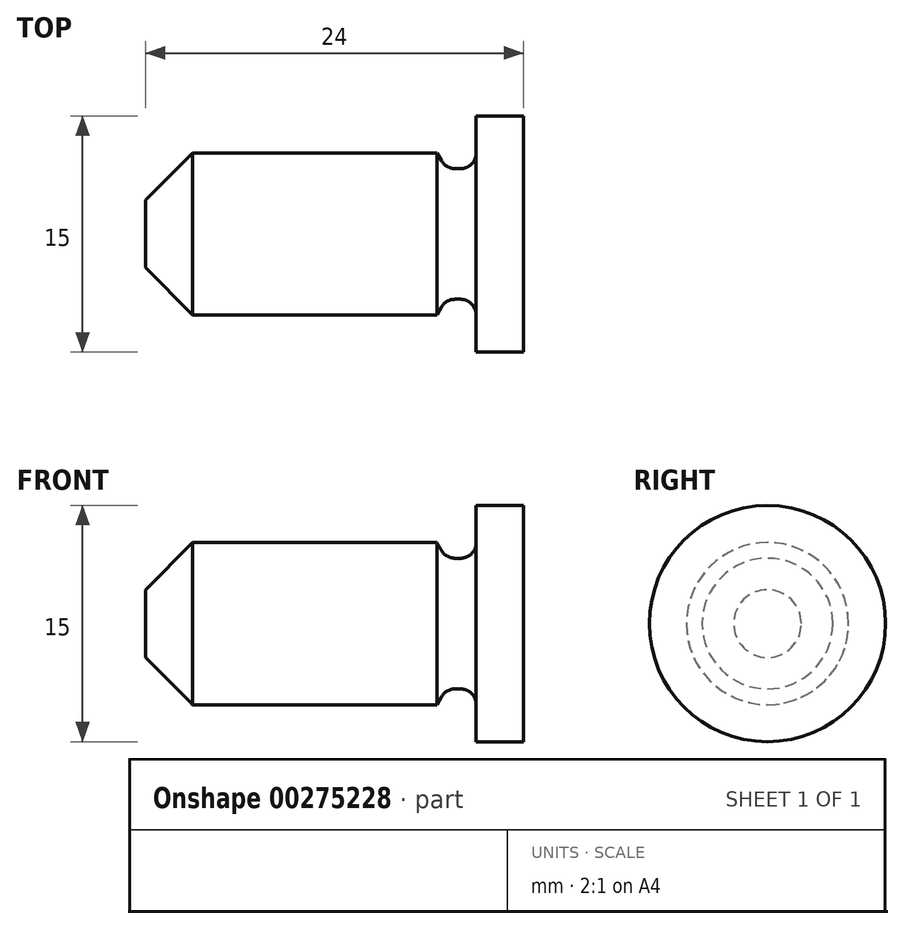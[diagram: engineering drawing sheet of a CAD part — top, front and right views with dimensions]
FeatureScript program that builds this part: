
annotation { "Feature Type Name" : "Feature", "Feature Type Description" : "" }
export const myFeature = defineFeature(function(context is Context, id is Id, definition is map)
    precondition{}
    {
        {
            var Q0;
            Q0=qCreatedBy(makeId("Front.planeOp"),FACE);
            var sketch = newSketch(context, id + "F0", { "sketchPlane" : qUnion([Q0])});
            skLineSegment(sketch, "E0", {"start": v(0, 5.15) * mm, "end": v(18.5, 5.15) * mm});
            skLineSegment(sketch, "E1", {"start": v(18.5, 5.15) * mm, "end": v(21, 5.15) * mm, "construction": true});
            skLineSegment(sketch, "E2", {"start": v(21, 5.15) * mm, "end": v(21, 7.5) * mm});
            skLineSegment(sketch, "E3", {"start": v(21, 7.5) * mm, "end": v(24, 7.5) * mm});
            skLineSegment(sketch, "E4", {"start": v(24, 7.5) * mm, "end": v(24, 0) * mm});
            skLineSegment(sketch, "E5", {"start": v(0, 5.15) * mm, "end": v(0, 0) * mm});
            skLineSegment(sketch, "E6.MirrorCS", {"start": v(18.5, -5.15) * mm, "end": v(21, -5.15) * mm, "construction": true});
            skLineSegment(sketch, "E7.MirrorCS", {"start": v(0, -5.15) * mm, "end": v(0, 0) * mm, "construction": true});
            skLineSegment(sketch, "E8.MirrorCS", {"start": v(0, -5.15) * mm, "end": v(18.5, -5.15) * mm, "construction": true});
            skLineSegment(sketch, "E9.MirrorCS", {"start": v(21, -7.5) * mm, "end": v(24, -7.5) * mm, "construction": true});
            skLineSegment(sketch, "E10.MirrorCS", {"start": v(24, -7.5) * mm, "end": v(24, 0) * mm, "construction": true});
            skLineSegment(sketch, "E11.MirrorCS", {"start": v(21, -5.15) * mm, "end": v(21, -7.5) * mm, "construction": true});
            skLineSegment(sketch, "E12", {"start": v(19.65, 4.15) * mm, "end": v(20, 4.15) * mm});
            skArc(sketch, "E13", {"start": v(20, 4.15) * mm, "mid": v(20.7, 4.44) * mm, "end": v(21, 5.15) * mm});
            skLineSegment(sketch, "E14", {"start": v(18.5, 5.15) * mm, "end": v(18.79, 4.65) * mm});
            skLineSegment(sketch, "E15.MirrorCS", {"start": v(19.65, -4.15) * mm, "end": v(20, -4.15) * mm, "construction": true});
            skArc(sketch, "E16", {"start": v(18.79, 4.65) * mm, "mid": v(19.15, 4.28) * mm, "end": v(19.65, 4.15) * mm});
            skArc(sketch, "E17.MirrorCS", {"start": v(20, -4.15) * mm, "mid": v(20.7, -4.44) * mm, "end": v(21, -5.15) * mm, "construction": true});
            skArc(sketch, "E18.MirrorCS", {"start": v(18.79, -4.65) * mm, "mid": v(19.15, -4.28) * mm, "end": v(19.65, -4.15) * mm, "construction": true});
            skLineSegment(sketch, "E19.MirrorCS", {"start": v(18.5, -5.15) * mm, "end": v(18.79, -4.65) * mm, "construction": true});
            skLineSegment(sketch, "E20", {"start": v(-4.5, 0) * mm, "end": v(29.21, 0) * mm});
            skSolve(sketch);
        }
        {
            var Q0;
            Q0=makeQuery(id+"F0.imprint","IMPRINT",FACE,{"disambiguationData":[TD([[makeQuery(id+"F0.imprint","IMPRINT",EDGE,{"derivedFrom":sQuery(id+"F0.wireOp",EDGE,"E0")}),-1.0]])]});
            var Q1;
            Q1=sQuery(id+"F0.wireOp",EDGE,"E20");
            revolve(context, id + "F1", {"entities" : qUnion([Q0]), "axis" : qUnion([Q1]), "revolveType" : RevolveType.FULL});
        }
        {
            var Q0;
            Q0=makeQuery(id+"F1.opRevolve","SWEPT_EDGE",EDGE,{"disambiguationData":[OSD([sQuery(id+"F0.wireOp",EDGE,"E0"),sQuery(id+"F0.wireOp",EDGE,"E5")])]});
            chamfer(context, id + "F2", {"entities" : qUnion([Q0]), "chamferType" : ChamferType.OFFSET_ANGLE, "width" : 3 * mm, "oppositeDirection" : false, "angle" : 45 * degree});
        }
    });
